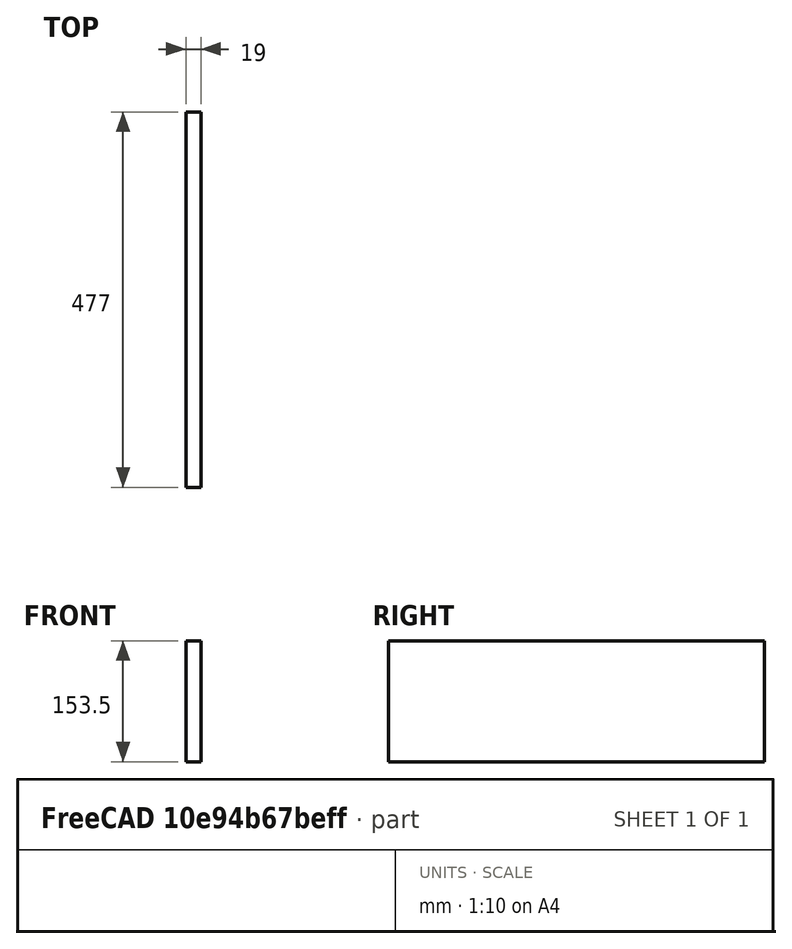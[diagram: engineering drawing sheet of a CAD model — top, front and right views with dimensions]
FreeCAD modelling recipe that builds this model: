
FCSTD DOCUMENT  (FreeCAD 1.0RUnknown)
Label: drawer_back
License: All rights reserved
objects: PartDesign::CoordinateSystem×2, Sketcher::SketchObject×1, PartDesign::Pad×1, PartDesign::Body×1
note: 8 computed .brp shape members not serialized (recipe doc carries the construction recipe); baked Part::Feature solids carry a one-line shape summary decoded from their .brp
EXTERNAL_REF file=../../mastersketch.FCStd obj=Spreadsheet

FEATURE [Sketcher::SketchObject] Sketch
  ArcFitTolerance = 1e-06
  AttachmentSupport = -> [XZ_Plane]
  FullyConstrained = true
  MakeInternals = false
  MapMode = 5
  Placement = pos=(0,0,0) rot=(1,0,0;1.5708rad)
  expr: Constraints[10] = mastersketch#Spreadsheet.drawer_outer_thickness
  expr: Constraints[11] = mastersketch#Spreadsheet.drawer_height - (mastersketch#Spreadsheet.drawer_bottom_thickness + mastersketch#Spreadsheet.drawer_bottom_tol + mastersketch#Spreadsheet.drawer_slot_height)
  sketch-geometry (5):
    g0: LineSegment StartX=-9.5 StartY=-76.75 StartZ=0 EndX=9.5 EndY=-76.75 EndZ=0
    g1: LineSegment StartX=9.5 StartY=-76.75 StartZ=0 EndX=9.5 EndY=76.75 EndZ=0
    g2: LineSegment StartX=9.5 StartY=76.75 StartZ=0 EndX=-9.5 EndY=76.75 EndZ=0
    g3: LineSegment StartX=-9.5 StartY=76.75 StartZ=0 EndX=-9.5 EndY=-76.75 EndZ=0
    g4: GeomPoint [constr] X=0 Y=0 Z=0
  constraints (12):
    c: Coincident(g0,g1)
    c: Coincident(g1,g2)
    c: Coincident(g2,g3)
    c: Coincident(g3,g0)
    c: Horizontal(g0)
    c: Horizontal(g2)
    c: Vertical(g1)
    c: Vertical(g3)
    c: Symmetric(g2,g0,g4)
    c: Coincident(g4,g-1)
    c: DistanceX(g0,g0) = 19
    c: DistanceY(g1,g1) = 153.5
FEATURE [PartDesign::Pad] Pad
  Direction = (0,-1,2e-16)
  Length = 477
  Length2 = 10
  Placement = pos=(0,0,0) rot=(1,0,0;1.5708rad)
  Profile = -> Sketch
  ReferenceAxis = -> Sketch [N_Axis]
  Refine = true
  Suppressed = false
  Type = 0
  expr: Length = mastersketch#Spreadsheet.drawer_width
FEATURE [PartDesign::CoordinateSystem] LCS_left
  AttacherType = Attacher::AttachEngine3D
  AttachmentSupport = -> [Pad]
  MapMode = 7
  Placement = pos=(9.5,-477,76.75) rot=(0,1,0;3.14159rad)
FEATURE [PartDesign::CoordinateSystem] LCS_right
  AttacherType = Attacher::AttachEngine3D
  AttachmentSupport = -> [Pad]
  MapMode = 7
  Placement = pos=(9.5,0,76.75) rot=(0,1,0;3.14159rad)
FEATURE [PartDesign::Body] Body  label="drawer_back"
  AllowCompound = false
  Group = -> [Sketch,Pad,LCS_left,LCS_right]
  Origin = -> Origin
  Tip = -> Pad
